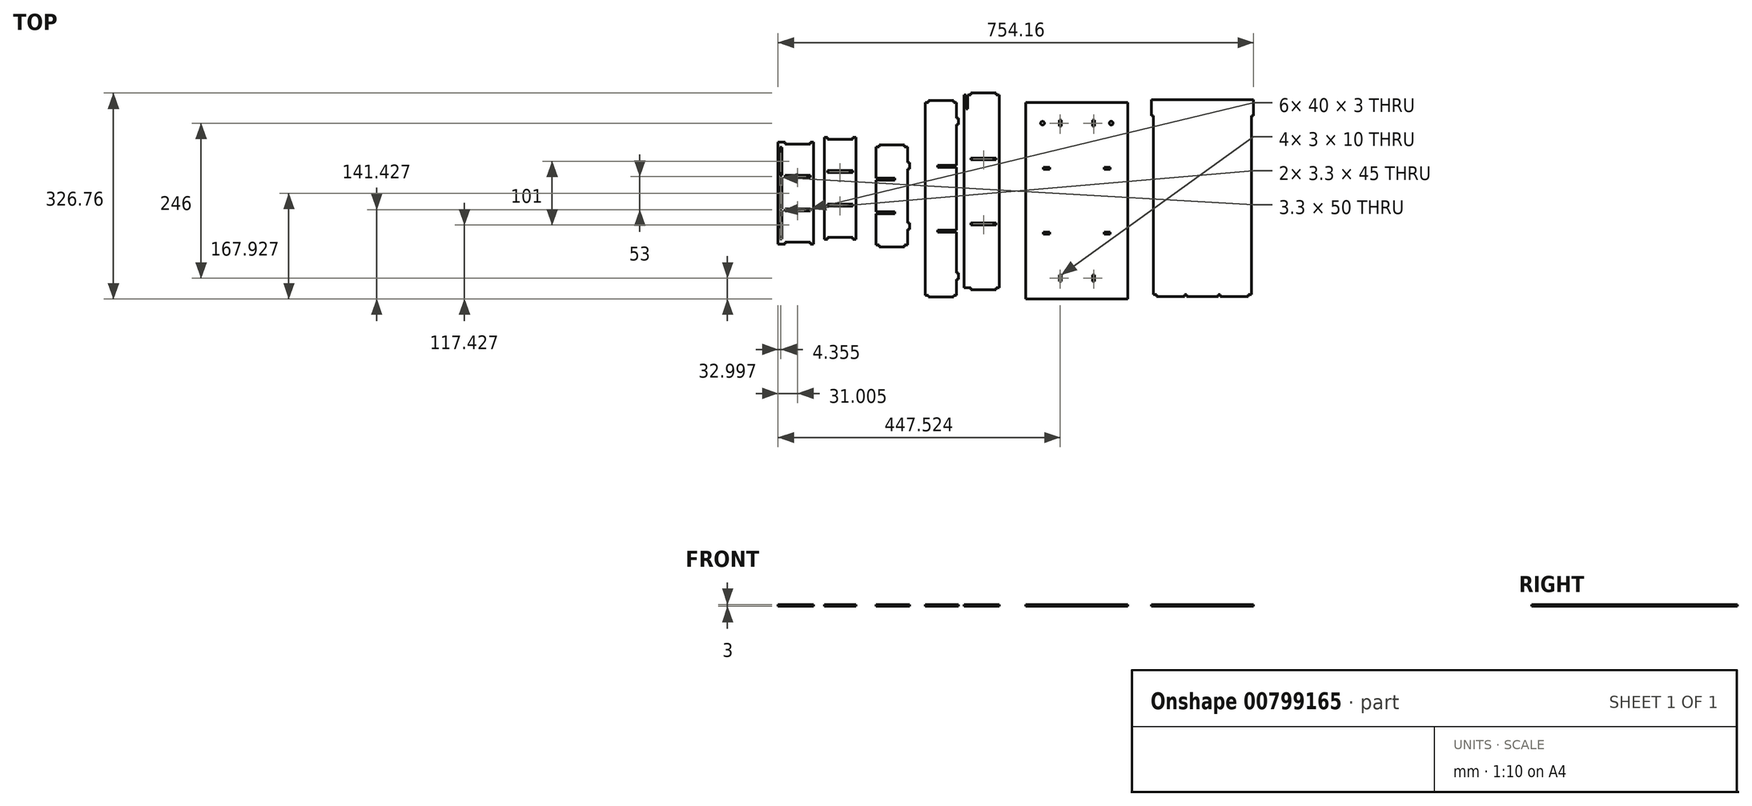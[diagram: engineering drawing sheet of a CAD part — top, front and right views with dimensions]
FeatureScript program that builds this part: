
annotation { "Feature Type Name" : "Feature", "Feature Type Description" : "" }
export const myFeature = defineFeature(function(context is Context, id is Id, definition is map)
    precondition{}
    {
        {
            var Q0;
            Q0=qCreatedBy(makeId("Top.planeOp"),FACE);
            var sketch = newSketch(context, id + "F0", { "sketchPlane" : qUnion([Q0])});
            skLineSegment(sketch, "E0.bottom", {"start": v(-53.58, 94.26) * mm, "end": v(-13.58, 94.26) * mm});
            skLineSegment(sketch, "E0.top", {"start": v(-53.58, -67.74) * mm, "end": v(-13.58, -67.74) * mm});
            skLineSegment(sketch, "E0.left", {"start": v(-58.58, 91.26) * mm, "end": v(-58.58, 41.26) * mm});
            skLineSegment(sketch, "E0.right", {"start": v(-8.58, 91.26) * mm, "end": v(-8.58, 66.26) * mm});
            skLineSegment(sketch, "E1", {"start": v(-58.58, 91.26) * mm, "end": v(-53.58, 91.26) * mm});
            skLineSegment(sketch, "E2", {"start": v(-53.58, 91.26) * mm, "end": v(-53.58, 94.26) * mm});
            skLineSegment(sketch, "E3", {"start": v(-13.58, 94.26) * mm, "end": v(-13.58, 91.26) * mm});
            skLineSegment(sketch, "E4", {"start": v(-13.58, 91.26) * mm, "end": v(-8.58, 91.26) * mm});
            skLineSegment(sketch, "E5", {"start": v(-58.58, -64.74) * mm, "end": v(-53.58, -64.74) * mm});
            skLineSegment(sketch, "E6", {"start": v(-53.58, -64.74) * mm, "end": v(-53.58, -67.74) * mm});
            skLineSegment(sketch, "E7", {"start": v(-8.58, -64.74) * mm, "end": v(-13.58, -64.74) * mm});
            skLineSegment(sketch, "E8", {"start": v(-13.58, -64.74) * mm, "end": v(-13.58, -67.74) * mm});
            skLineSegment(sketch, "E9", {"start": v(-58.58, 41.26) * mm, "end": v(-28.58, 41.26) * mm});
            skLineSegment(sketch, "E10", {"start": v(-28.58, 41.26) * mm, "end": v(-28.58, 38.26) * mm});
            skLineSegment(sketch, "E11", {"start": v(-28.58, 38.26) * mm, "end": v(-58.58, 38.26) * mm});
            skLineSegment(sketch, "E12", {"start": v(-58.58, -11.74) * mm, "end": v(-28.58, -11.74) * mm});
            skLineSegment(sketch, "E13", {"start": v(-28.58, -11.74) * mm, "end": v(-28.58, -14.74) * mm});
            skLineSegment(sketch, "E14", {"start": v(-28.58, -14.74) * mm, "end": v(-58.58, -14.74) * mm});
            skLineSegment(sketch, "E15.trimOffspring", {"start": v(-58.58, 38.26) * mm, "end": v(-58.58, -11.74) * mm});
            skLineSegment(sketch, "E16.trimOffspring", {"start": v(-58.58, -14.74) * mm, "end": v(-58.58, -64.74) * mm});
            skLineSegment(sketch, "E17", {"start": v(-8.58, 66.26) * mm, "end": v(-5.58, 66.26) * mm});
            skLineSegment(sketch, "E18", {"start": v(-5.58, 66.26) * mm, "end": v(-5.58, 56.26) * mm});
            skLineSegment(sketch, "E19", {"start": v(-5.58, 56.26) * mm, "end": v(-8.58, 56.26) * mm});
            skLineSegment(sketch, "E20", {"start": v(-8.58, -29.74) * mm, "end": v(-5.58, -29.74) * mm});
            skLineSegment(sketch, "E21", {"start": v(-5.58, -29.74) * mm, "end": v(-5.58, -39.74) * mm});
            skLineSegment(sketch, "E22", {"start": v(-5.58, -39.74) * mm, "end": v(-8.58, -39.74) * mm});
            skLineSegment(sketch, "E23.trimOffspring", {"start": v(-8.58, 56.26) * mm, "end": v(-8.58, -29.74) * mm});
            skLineSegment(sketch, "E24.trimOffspring", {"start": v(-8.58, -39.74) * mm, "end": v(-8.58, -64.74) * mm});
            skSolve(sketch);
        }
        {
            var Q0;
            Q0 = qSketchRegion(id + "F0", true);
            extrude(context, id + "F1", {"entities" : qUnion([Q0]), "depth" : 3 * mm, "offsetDistance" : 25 * mm});
        }
        {
            var Q0;
            Q0=qCreatedBy(makeId("Top.planeOp"),FACE);
            var sketch = newSketch(context, id + "F2", { "sketchPlane" : qUnion([Q0])});
            skLineSegment(sketch, "E25.bottom", {"start": v(24.28, 164.7) * mm, "end": v(64.28, 164.7) * mm});
            skLineSegment(sketch, "E25.top", {"start": v(24.28, -147.3) * mm, "end": v(64.28, -147.3) * mm});
            skLineSegment(sketch, "E25.right", {"start": v(69.28, 161.7) * mm, "end": v(69.28, 136.7) * mm});
            skLineSegment(sketch, "E26", {"start": v(19.28, 161.7) * mm, "end": v(24.28, 161.7) * mm});
            skLineSegment(sketch, "E27", {"start": v(24.28, 161.7) * mm, "end": v(24.28, 164.7) * mm});
            skLineSegment(sketch, "E28", {"start": v(64.28, 164.7) * mm, "end": v(64.28, 161.7) * mm});
            skLineSegment(sketch, "E29", {"start": v(64.28, 161.7) * mm, "end": v(69.28, 161.7) * mm});
            skLineSegment(sketch, "E30", {"start": v(19.28, -144.3) * mm, "end": v(24.28, -144.3) * mm});
            skLineSegment(sketch, "E31", {"start": v(24.28, -144.3) * mm, "end": v(24.28, -147.3) * mm});
            skLineSegment(sketch, "E32", {"start": v(69.28, -144.3) * mm, "end": v(64.28, -144.3) * mm});
            skLineSegment(sketch, "E33", {"start": v(64.28, -144.3) * mm, "end": v(64.28, -147.3) * mm});
            skLineSegment(sketch, "E34", {"start": v(69.28, 136.7) * mm, "end": v(72.28, 136.7) * mm});
            skLineSegment(sketch, "E35", {"start": v(72.28, 136.7) * mm, "end": v(72.28, 126.7) * mm});
            skLineSegment(sketch, "E36", {"start": v(72.28, 126.7) * mm, "end": v(69.28, 126.7) * mm});
            skLineSegment(sketch, "E37", {"start": v(69.28, -109.3) * mm, "end": v(72.28, -109.3) * mm});
            skLineSegment(sketch, "E38", {"start": v(72.28, -109.3) * mm, "end": v(72.28, -119.3) * mm});
            skLineSegment(sketch, "E39", {"start": v(72.28, -119.3) * mm, "end": v(69.28, -119.3) * mm});
            skLineSegment(sketch, "E40.trimOffspring", {"start": v(69.28, 126.7) * mm, "end": v(69.28, 61.7) * mm});
            skLineSegment(sketch, "E41.trimOffspring", {"start": v(69.28, -119.3) * mm, "end": v(69.28, -144.3) * mm});
            skLineSegment(sketch, "E42", {"start": v(19.28, 161.7) * mm, "end": v(19.28, -144.3) * mm});
            skLineSegment(sketch, "E43", {"start": v(69.28, 61.7) * mm, "end": v(39.28, 61.7) * mm});
            skLineSegment(sketch, "E44", {"start": v(39.28, 61.7) * mm, "end": v(39.28, 58.7) * mm});
            skLineSegment(sketch, "E45", {"start": v(39.28, 58.7) * mm, "end": v(69.28, 58.7) * mm});
            skLineSegment(sketch, "E46", {"start": v(69.28, -41.3) * mm, "end": v(39.28, -41.3) * mm});
            skLineSegment(sketch, "E47", {"start": v(39.28, -41.3) * mm, "end": v(39.28, -44.3) * mm});
            skLineSegment(sketch, "E48", {"start": v(39.28, -44.3) * mm, "end": v(69.28, -44.3) * mm});
            skLineSegment(sketch, "E49.trimOffspring", {"start": v(69.28, -44.3) * mm, "end": v(69.28, -109.3) * mm});
            skLineSegment(sketch, "E50.trimOffspring", {"start": v(69.28, 58.7) * mm, "end": v(69.28, -41.3) * mm});
            skSolve(sketch);
        }
        {
            var Q0;
            Q0 = qSketchRegion(id + "F2", true);
            extrude(context, id + "F3", {"entities" : qUnion([Q0]), "depth" : 3 * mm, "offsetDistance" : 25 * mm});
        }
        {
            var Q0;
            Q0=qCreatedBy(makeId("Top.planeOp"),FACE);
            var sketch = newSketch(context, id + "F4", { "sketchPlane" : qUnion([Q0])});
            skLineSegment(sketch, "E51.bottom", {"start": v(-140.63, 106.24) * mm, "end": v(-135.63, 106.24) * mm});
            skLineSegment(sketch, "E51.top", {"start": v(-140.63, -55.76) * mm, "end": v(-135.63, -55.76) * mm});
            skLineSegment(sketch, "E51.left", {"start": v(-140.63, 106.24) * mm, "end": v(-140.63, -55.76) * mm});
            skLineSegment(sketch, "E51.right", {"start": v(-90.63, 106.24) * mm, "end": v(-90.63, -55.76) * mm});
            skLineSegment(sketch, "E52.bottom", {"start": v(-135.63, 53.24) * mm, "end": v(-95.63, 53.24) * mm});
            skLineSegment(sketch, "E52.top", {"start": v(-135.63, 50.24) * mm, "end": v(-95.63, 50.24) * mm});
            skLineSegment(sketch, "E52.left", {"start": v(-135.63, 53.24) * mm, "end": v(-135.63, 50.24) * mm});
            skLineSegment(sketch, "E52.right", {"start": v(-95.63, 53.24) * mm, "end": v(-95.63, 50.24) * mm});
            skLineSegment(sketch, "E53.bottom", {"start": v(-135.63, 0.24) * mm, "end": v(-95.63, 0.24) * mm});
            skLineSegment(sketch, "E53.top", {"start": v(-135.63, -2.76) * mm, "end": v(-95.63, -2.76) * mm});
            skLineSegment(sketch, "E53.left", {"start": v(-135.63, 0.24) * mm, "end": v(-135.63, -2.76) * mm});
            skLineSegment(sketch, "E53.right", {"start": v(-95.63, 0.24) * mm, "end": v(-95.63, -2.76) * mm});
            skLineSegment(sketch, "E54", {"start": v(-135.63, 106.24) * mm, "end": v(-135.63, 103.24) * mm});
            skLineSegment(sketch, "E55", {"start": v(-135.63, 103.24) * mm, "end": v(-95.63, 103.24) * mm});
            skLineSegment(sketch, "E56", {"start": v(-95.63, 103.24) * mm, "end": v(-95.63, 106.24) * mm});
            skLineSegment(sketch, "E57.trimOffspring", {"start": v(-95.63, 106.24) * mm, "end": v(-90.63, 106.24) * mm});
            skLineSegment(sketch, "E58", {"start": v(-135.63, -55.76) * mm, "end": v(-135.63, -52.76) * mm});
            skLineSegment(sketch, "E59", {"start": v(-135.63, -52.76) * mm, "end": v(-95.63, -52.76) * mm});
            skLineSegment(sketch, "E60", {"start": v(-95.63, -52.76) * mm, "end": v(-95.63, -55.76) * mm});
            skLineSegment(sketch, "E61.trimOffspring", {"start": v(-95.63, -55.76) * mm, "end": v(-90.63, -55.76) * mm});
            skSolve(sketch);
        }
        {
            var Q0;
            Q0 = qSketchRegion(id + "F4", true);
            extrude(context, id + "F5", {"entities" : qUnion([Q0]), "depth" : 3 * mm, "offsetDistance" : 25 * mm});
        }
        {
            var Q0;
            Q0=qCreatedBy(makeId("Top.planeOp"),FACE);
            var sketch = newSketch(context, id + "F6", { "sketchPlane" : qUnion([Q0])});
            skLineSegment(sketch, "E62.bottom", {"start": v(-213.94, 98.68) * mm, "end": v(-202.94, 98.68) * mm});
            skLineSegment(sketch, "E62.top", {"start": v(-213.94, -63.32) * mm, "end": v(-202.94, -63.32) * mm});
            skLineSegment(sketch, "E62.left", {"start": v(-213.94, 98.68) * mm, "end": v(-213.94, -63.32) * mm});
            skLineSegment(sketch, "E62.right", {"start": v(-157.94, 98.68) * mm, "end": v(-157.94, -63.32) * mm});
            skLineSegment(sketch, "E63.bottom", {"start": v(-202.94, 45.68) * mm, "end": v(-162.94, 45.68) * mm});
            skLineSegment(sketch, "E63.top", {"start": v(-202.94, 42.68) * mm, "end": v(-162.94, 42.68) * mm});
            skLineSegment(sketch, "E63.left", {"start": v(-202.94, 45.68) * mm, "end": v(-202.94, 42.68) * mm});
            skLineSegment(sketch, "E63.right", {"start": v(-162.94, 45.68) * mm, "end": v(-162.94, 42.68) * mm});
            skLineSegment(sketch, "E64.bottom", {"start": v(-202.94, -7.32) * mm, "end": v(-162.94, -7.32) * mm});
            skLineSegment(sketch, "E64.top", {"start": v(-202.94, -10.32) * mm, "end": v(-162.94, -10.32) * mm});
            skLineSegment(sketch, "E64.left", {"start": v(-202.94, -7.32) * mm, "end": v(-202.94, -10.32) * mm});
            skLineSegment(sketch, "E64.right", {"start": v(-162.94, -7.32) * mm, "end": v(-162.94, -10.32) * mm});
            skLineSegment(sketch, "E65", {"start": v(-202.94, 98.68) * mm, "end": v(-202.94, 95.68) * mm});
            skLineSegment(sketch, "E66", {"start": v(-202.94, 95.68) * mm, "end": v(-162.94, 95.68) * mm});
            skLineSegment(sketch, "E67", {"start": v(-162.94, 95.68) * mm, "end": v(-162.94, 98.68) * mm});
            skLineSegment(sketch, "E68.trimOffspring", {"start": v(-162.94, 98.68) * mm, "end": v(-157.94, 98.68) * mm});
            skLineSegment(sketch, "E69", {"start": v(-202.94, -63.32) * mm, "end": v(-202.94, -60.32) * mm});
            skLineSegment(sketch, "E70", {"start": v(-202.94, -60.32) * mm, "end": v(-162.94, -60.32) * mm});
            skLineSegment(sketch, "E71", {"start": v(-162.94, -60.32) * mm, "end": v(-162.94, -63.32) * mm});
            skLineSegment(sketch, "E72.trimOffspring", {"start": v(-162.94, -63.32) * mm, "end": v(-157.94, -63.32) * mm});
            skLineSegment(sketch, "E73.bottom", {"start": v(-211.24, 90.68) * mm, "end": v(-207.94, 90.68) * mm});
            skLineSegment(sketch, "E73.top", {"start": v(-211.24, 45.68) * mm, "end": v(-207.94, 45.68) * mm});
            skLineSegment(sketch, "E73.left", {"start": v(-211.24, 90.68) * mm, "end": v(-211.24, 45.68) * mm});
            skLineSegment(sketch, "E73.right", {"start": v(-207.94, 90.68) * mm, "end": v(-207.94, 45.68) * mm});
            skLineSegment(sketch, "E74.bottom", {"start": v(-207.94, -7.32) * mm, "end": v(-211.24, -7.32) * mm});
            skLineSegment(sketch, "E74.top", {"start": v(-207.94, 42.68) * mm, "end": v(-211.24, 42.68) * mm});
            skLineSegment(sketch, "E74.left", {"start": v(-207.94, -7.32) * mm, "end": v(-207.94, 42.68) * mm});
            skLineSegment(sketch, "E74.right", {"start": v(-211.24, -7.32) * mm, "end": v(-211.24, 42.68) * mm});
            skLineSegment(sketch, "E75.bottom", {"start": v(-207.94, -10.32) * mm, "end": v(-211.24, -10.32) * mm});
            skLineSegment(sketch, "E75.top", {"start": v(-207.94, -55.32) * mm, "end": v(-211.24, -55.32) * mm});
            skLineSegment(sketch, "E75.left", {"start": v(-207.94, -10.32) * mm, "end": v(-207.94, -55.32) * mm});
            skLineSegment(sketch, "E75.right", {"start": v(-211.24, -10.32) * mm, "end": v(-211.24, -55.32) * mm});
            skSolve(sketch);
        }
        {
            var Q0;
            Q0 = qSketchRegion(id + "F6", true);
            extrude(context, id + "F7", {"entities" : qUnion([Q0]), "depth" : 3 * mm, "offsetDistance" : 25 * mm});
        }
        {
            var Q0;
            Q0=qCreatedBy(makeId("Top.planeOp"),FACE);
            var sketch = newSketch(context, id + "F8", { "sketchPlane" : qUnion([Q0])});
            skLineSegment(sketch, "E76.bottom", {"start": v(92.04, 176.51) * mm, "end": v(132.04, 176.51) * mm});
            skLineSegment(sketch, "E76.top", {"start": v(92.04, -135.49) * mm, "end": v(132.04, -135.49) * mm});
            skLineSegment(sketch, "E77", {"start": v(92.04, 173.51) * mm, "end": v(92.04, 176.51) * mm});
            skLineSegment(sketch, "E78", {"start": v(132.04, 176.51) * mm, "end": v(132.04, 173.51) * mm});
            skLineSegment(sketch, "E79", {"start": v(132.04, 173.51) * mm, "end": v(137.04, 173.51) * mm});
            skLineSegment(sketch, "E80", {"start": v(81.04, -132.49) * mm, "end": v(92.04, -132.49) * mm});
            skLineSegment(sketch, "E81", {"start": v(92.04, -132.49) * mm, "end": v(92.04, -135.49) * mm});
            skLineSegment(sketch, "E82", {"start": v(137.04, -132.49) * mm, "end": v(132.04, -132.49) * mm});
            skLineSegment(sketch, "E83", {"start": v(132.04, -132.49) * mm, "end": v(132.04, -135.49) * mm});
            skLineSegment(sketch, "E84", {"start": v(81.04, 173.51) * mm, "end": v(81.04, -132.49) * mm});
            skLineSegment(sketch, "E85", {"start": v(137.04, 173.51) * mm, "end": v(137.04, -132.49) * mm});
            skLineSegment(sketch, "E86.bottom", {"start": v(92.04, 73.51) * mm, "end": v(132.04, 73.51) * mm});
            skLineSegment(sketch, "E86.top", {"start": v(92.04, 70.51) * mm, "end": v(132.04, 70.51) * mm});
            skLineSegment(sketch, "E86.left", {"start": v(92.04, 73.51) * mm, "end": v(92.04, 70.51) * mm});
            skLineSegment(sketch, "E86.right", {"start": v(132.04, 73.51) * mm, "end": v(132.04, 70.51) * mm});
            skLineSegment(sketch, "E87.bottom", {"start": v(92.04, -29.49) * mm, "end": v(132.04, -29.49) * mm});
            skLineSegment(sketch, "E87.top", {"start": v(92.04, -32.49) * mm, "end": v(132.04, -32.49) * mm});
            skLineSegment(sketch, "E87.left", {"start": v(92.04, -29.49) * mm, "end": v(92.04, -32.49) * mm});
            skLineSegment(sketch, "E87.right", {"start": v(132.04, -29.49) * mm, "end": v(132.04, -32.49) * mm});
            skLineSegment(sketch, "E88", {"start": v(87.04, 151.51) * mm, "end": v(87.04, 173.51) * mm});
            skLineSegment(sketch, "E89.trimOffspring", {"start": v(87.04, 173.51) * mm, "end": v(92.04, 173.51) * mm});
            skLineSegment(sketch, "E90", {"start": v(81.04, 173.51) * mm, "end": v(83.94, 173.51) * mm});
            skLineSegment(sketch, "E91", {"start": v(83.94, 173.51) * mm, "end": v(83.94, 151.51) * mm});
            skLineSegment(sketch, "E92", {"start": v(83.94, 151.51) * mm, "end": v(87.04, 151.51) * mm});
            skSolve(sketch);
        }
        {
            var Q0;
            Q0 = qSketchRegion(id + "F8", true);
            extrude(context, id + "F9", {"entities" : qUnion([Q0]), "depth" : 3 * mm, "offsetDistance" : 25 * mm});
        }
        {
            var Q0;
            Q0=qCreatedBy(makeId("Top.planeOp"),FACE);
            var sketch = newSketch(context, id + "F10", { "sketchPlane" : qUnion([Q0])});
            skLineSegment(sketch, "E93.bottom", {"start": v(179.08, 161.75) * mm, "end": v(341.08, 161.75) * mm});
            skLineSegment(sketch, "E93.top", {"start": v(179.08, -150.25) * mm, "end": v(341.08, -150.25) * mm});
            skLineSegment(sketch, "E93.left", {"start": v(179.08, 161.75) * mm, "end": v(179.08, -150.25) * mm});
            skLineSegment(sketch, "E93.right", {"start": v(341.08, 161.75) * mm, "end": v(341.08, -150.25) * mm});
            skLineSegment(sketch, "E94.bottom", {"start": v(232.08, 133.75) * mm, "end": v(235.08, 133.75) * mm});
            skLineSegment(sketch, "E94.top", {"start": v(232.08, 123.75) * mm, "end": v(235.08, 123.75) * mm});
            skLineSegment(sketch, "E94.left", {"start": v(232.08, 133.75) * mm, "end": v(232.08, 123.75) * mm});
            skLineSegment(sketch, "E94.right", {"start": v(235.08, 133.75) * mm, "end": v(235.08, 123.75) * mm});
            skLineSegment(sketch, "E95.bottom", {"start": v(285.08, 133.75) * mm, "end": v(288.08, 133.75) * mm});
            skLineSegment(sketch, "E95.top", {"start": v(285.08, 123.75) * mm, "end": v(288.08, 123.75) * mm});
            skLineSegment(sketch, "E95.left", {"start": v(285.08, 133.75) * mm, "end": v(285.08, 123.75) * mm});
            skLineSegment(sketch, "E95.right", {"start": v(288.08, 133.75) * mm, "end": v(288.08, 123.75) * mm});
            skLineSegment(sketch, "E96.bottom", {"start": v(303.08, 58.75) * mm, "end": v(313.08, 58.75) * mm});
            skLineSegment(sketch, "E96.top", {"start": v(303.08, 55.75) * mm, "end": v(313.08, 55.75) * mm});
            skLineSegment(sketch, "E96.left", {"start": v(303.08, 58.75) * mm, "end": v(303.08, 55.75) * mm});
            skLineSegment(sketch, "E96.right", {"start": v(313.08, 58.75) * mm, "end": v(313.08, 55.75) * mm});
            skLineSegment(sketch, "E97.bottom", {"start": v(303.08, -44.25) * mm, "end": v(313.08, -44.25) * mm});
            skLineSegment(sketch, "E97.top", {"start": v(303.08, -47.25) * mm, "end": v(313.08, -47.25) * mm});
            skLineSegment(sketch, "E97.left", {"start": v(303.08, -44.25) * mm, "end": v(303.08, -47.25) * mm});
            skLineSegment(sketch, "E97.right", {"start": v(313.08, -44.25) * mm, "end": v(313.08, -47.25) * mm});
            skLineSegment(sketch, "E98.bottom", {"start": v(217.08, 58.75) * mm, "end": v(207.08, 58.75) * mm});
            skLineSegment(sketch, "E98.top", {"start": v(217.08, 55.75) * mm, "end": v(207.08, 55.75) * mm});
            skLineSegment(sketch, "E98.left", {"start": v(217.08, 58.75) * mm, "end": v(217.08, 55.75) * mm});
            skLineSegment(sketch, "E98.right", {"start": v(207.08, 58.75) * mm, "end": v(207.08, 55.75) * mm});
            skLineSegment(sketch, "E99.bottom", {"start": v(217.08, -44.25) * mm, "end": v(207.08, -44.25) * mm});
            skLineSegment(sketch, "E99.top", {"start": v(217.08, -47.25) * mm, "end": v(207.08, -47.25) * mm});
            skLineSegment(sketch, "E99.left", {"start": v(217.08, -44.25) * mm, "end": v(217.08, -47.25) * mm});
            skLineSegment(sketch, "E99.right", {"start": v(207.08, -44.25) * mm, "end": v(207.08, -47.25) * mm});
            skLineSegment(sketch, "E100.bottom", {"start": v(232.08, -112.25) * mm, "end": v(235.08, -112.25) * mm});
            skLineSegment(sketch, "E100.top", {"start": v(232.08, -122.25) * mm, "end": v(235.08, -122.25) * mm});
            skLineSegment(sketch, "E100.left", {"start": v(232.08, -112.25) * mm, "end": v(232.08, -122.25) * mm});
            skLineSegment(sketch, "E100.right", {"start": v(235.08, -112.25) * mm, "end": v(235.08, -122.25) * mm});
            skLineSegment(sketch, "E101.bottom", {"start": v(285.08, -112.25) * mm, "end": v(288.08, -112.25) * mm});
            skLineSegment(sketch, "E101.top", {"start": v(285.08, -122.25) * mm, "end": v(288.08, -122.25) * mm});
            skLineSegment(sketch, "E101.left", {"start": v(285.08, -112.25) * mm, "end": v(285.08, -122.25) * mm});
            skLineSegment(sketch, "E101.right", {"start": v(288.08, -112.25) * mm, "end": v(288.08, -122.25) * mm});
            skCircle(sketch, "E102", {"center": v(205.58, 128.75) * mm, "radius": 3 * mm});
            skCircle(sketch, "E103", {"center": v(314.58, 128.75) * mm, "radius": 3 * mm});
            skSolve(sketch);
        }
        {
            var Q0;
            Q0=makeQuery(id+"F10.imprint","IMPRINT",FACE,{"disambiguationData":[TD([[makeQuery(id+"F10.imprint","IMPRINT",EDGE,{"derivedFrom":sQuery(id+"F10.wireOp",EDGE,"E93.bottom")}),-1.0]])]});
            extrude(context, id + "F11", {"entities" : qUnion([Q0]), "depth" : 3 * mm, "offsetDistance" : 25 * mm});
        }
        {
            var Q0;
            Q0=qCreatedBy(makeId("Top.planeOp"),FACE);
            var sketch = newSketch(context, id + "F12", { "sketchPlane" : qUnion([Q0])});
            skLineSegment(sketch, "E104.bottom", {"start": v(378.22, 165.65) * mm, "end": v(540.22, 165.65) * mm});
            skLineSegment(sketch, "E104.top", {"start": v(386.32, -146.35) * mm, "end": v(431.12, -146.35) * mm});
            skLineSegment(sketch, "E104.left", {"start": v(378.22, 165.65) * mm, "end": v(378.22, 140.65) * mm});
            skLineSegment(sketch, "E104.right", {"start": v(540.22, 165.65) * mm, "end": v(540.22, 140.65) * mm});
            skLineSegment(sketch, "E105", {"start": v(378.22, 140.65) * mm, "end": v(381.22, 140.65) * mm});
            skLineSegment(sketch, "E106", {"start": v(381.22, 140.65) * mm, "end": v(381.22, -143.35) * mm});
            skLineSegment(sketch, "E107", {"start": v(540.22, 140.65) * mm, "end": v(537.22, 140.65) * mm});
            skLineSegment(sketch, "E108", {"start": v(537.22, 140.65) * mm, "end": v(537.22, -143.35) * mm});
            skLineSegment(sketch, "E109", {"start": v(431.12, -146.35) * mm, "end": v(431.12, -143.35) * mm});
            skLineSegment(sketch, "E110", {"start": v(431.12, -143.35) * mm, "end": v(434.32, -143.35) * mm});
            skLineSegment(sketch, "E111", {"start": v(434.32, -143.35) * mm, "end": v(434.32, -146.35) * mm});
            skLineSegment(sketch, "E112", {"start": v(484.12, -146.35) * mm, "end": v(484.12, -143.35) * mm});
            skLineSegment(sketch, "E113", {"start": v(484.12, -143.35) * mm, "end": v(487.32, -143.35) * mm});
            skLineSegment(sketch, "E114", {"start": v(487.32, -143.35) * mm, "end": v(487.32, -146.35) * mm});
            skLineSegment(sketch, "E115.trimOffspring", {"start": v(434.32, -146.35) * mm, "end": v(484.12, -146.35) * mm});
            skLineSegment(sketch, "E116.trimOffspring", {"start": v(487.32, -146.35) * mm, "end": v(532.12, -146.35) * mm});
            skLineSegment(sketch, "E117", {"start": v(381.22, -143.35) * mm, "end": v(386.32, -143.35) * mm});
            skLineSegment(sketch, "E118", {"start": v(386.32, -143.35) * mm, "end": v(386.32, -146.35) * mm});
            skLineSegment(sketch, "E119", {"start": v(537.22, -143.35) * mm, "end": v(532.12, -143.35) * mm});
            skLineSegment(sketch, "E120", {"start": v(532.12, -143.35) * mm, "end": v(532.12, -146.35) * mm});
            skSolve(sketch);
        }
        {
            var Q0;
            Q0 = qSketchRegion(id + "F12", true);
            extrude(context, id + "F13", {"entities" : qUnion([Q0]), "depth" : 3 * mm, "offsetDistance" : 25 * mm});
        }
    });
